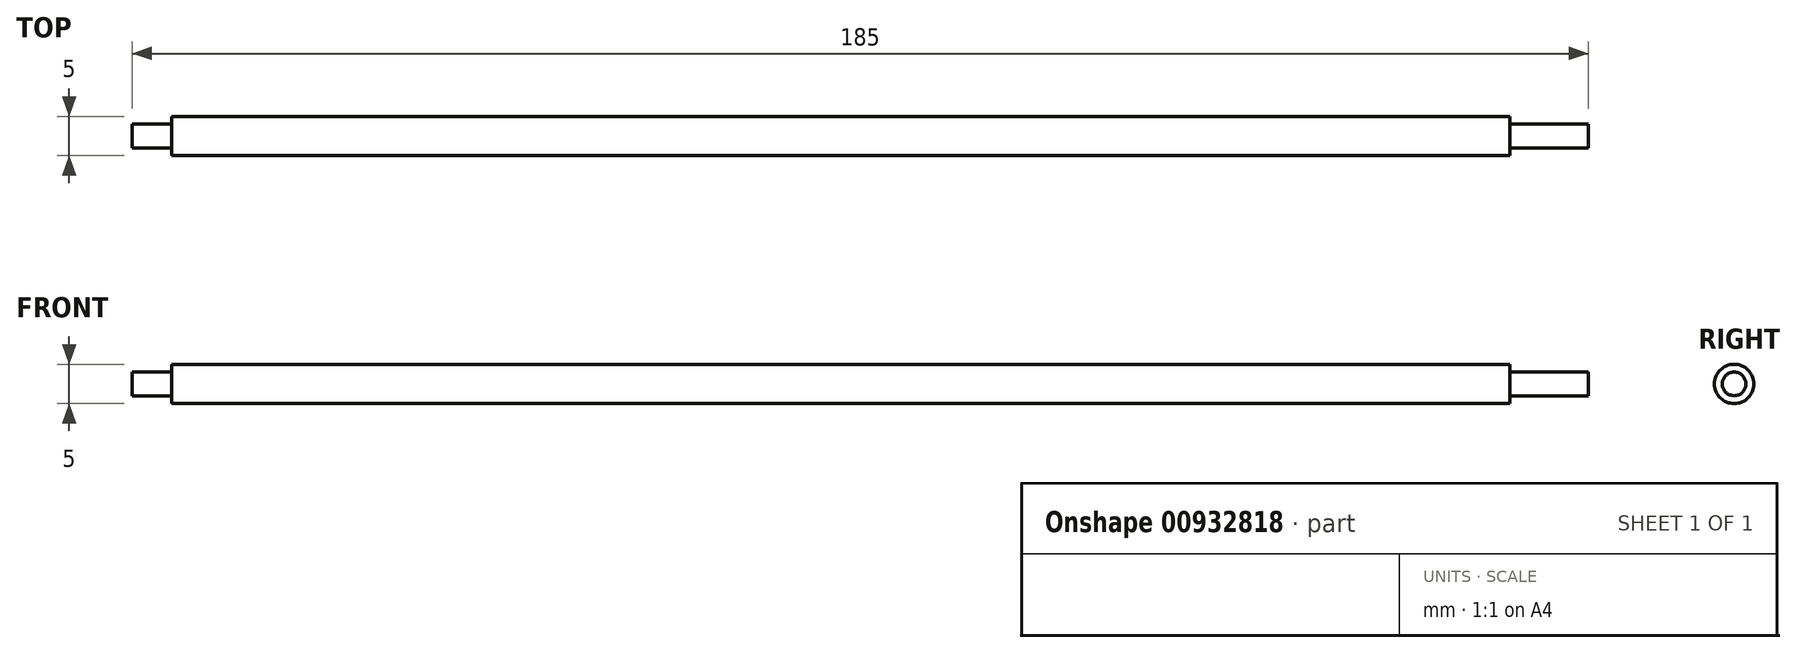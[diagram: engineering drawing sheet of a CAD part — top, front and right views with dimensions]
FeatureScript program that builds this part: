
annotation { "Feature Type Name" : "Feature", "Feature Type Description" : "" }
export const myFeature = defineFeature(function(context is Context, id is Id, definition is map)
    precondition{}
    {
        {
            var Q0;
            Q0=qCreatedBy(makeId("Front.planeOp"),FACE);
            var sketch = newSketch(context, id + "F0", { "sketchPlane" : qUnion([Q0])});
            skLineSegment(sketch, "E0", {"start": v(-38.43, 0) * mm, "end": v(-38.43, 1.5) * mm});
            skLineSegment(sketch, "E1", {"start": v(-38.43, 1.5) * mm, "end": v(-33.43, 1.5) * mm});
            skLineSegment(sketch, "E2", {"start": v(-33.43, 1.5) * mm, "end": v(-33.43, 2.5) * mm});
            skLineSegment(sketch, "E3", {"start": v(-33.43, 2.5) * mm, "end": v(136.57, 2.5) * mm});
            skLineSegment(sketch, "E4", {"start": v(136.57, 2.5) * mm, "end": v(136.57, 1.5) * mm});
            skLineSegment(sketch, "E5", {"start": v(136.57, 1.5) * mm, "end": v(146.57, 1.5) * mm});
            skLineSegment(sketch, "E6", {"start": v(146.57, 1.5) * mm, "end": v(146.57, 0) * mm});
            skLineSegment(sketch, "E7", {"start": v(146.57, 0) * mm, "end": v(-38.43, 0) * mm});
            skSolve(sketch);
        }
        {
            var Q0;
            Q0=makeQuery(id+"F0.imprint","IMPRINT",FACE,{"disambiguationData":[TD([[makeQuery(id+"F0.imprint","IMPRINT",EDGE,{"derivedFrom":sQuery(id+"F0.wireOp",EDGE,"E0")}),-1.0]])]});
            var Q1;
            Q1=sQuery(id+"F0.wireOp",EDGE,"E7");
            revolve(context, id + "F1", {"surfaceOperationType" : NewSurfaceOperationType.NEW, "entities" : qUnion([Q0]), "axis" : qUnion([Q1]), "revolveType" : RevolveType.FULL});
        }
    });
